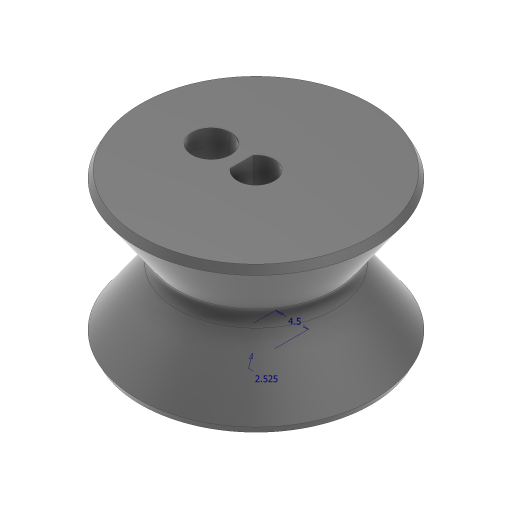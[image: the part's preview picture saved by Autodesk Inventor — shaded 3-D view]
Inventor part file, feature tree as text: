
AUTODESK INVENTOR PART (.ipt)
format: ipt  version: 2023 (Build 270158000, 158)  size: 294,912 bytes
history: native  units: mm
features: sketch x3, chamfer x3, plane x2, revolve x1, extrude x1, sweep x1, fillet x1, hole x1
ambient origin geometry x8: Origin, YZ Plane, XZ Plane, XY Plane, X Axis, Y Axis, Z Axis, Center Point
bodies: Solid1 (feature_tree)
feature tree (13):
  sketch  "Sketch1"  dims[d1=4.5mm d4=20.0mm]
  revolve  "Revolution1"  [1 undecoded]
  extrude  "Extrusion1"  Depth=14.0mm
  chamfer  "Chamfer1"  [1 undecoded]
  plane  "Work Plane3"
  sweep  "Sweep1"
  plane  "Work Plane4"
  fillet  "Fillet1"  Radius=3.490659mm
  chamfer  "Chamfer2"  [1 undecoded]
  hole  "Hole4"  [1 undecoded]
  chamfer  "Chamfer3"  [1 undecoded]
  sketch  "Sketch8"  dims[d5=14.0mm d6=14.0mm]
  sketch  "Sketch9"  dims[d7=90.0deg d8=0.0mm d9=0.0mm d10=1.2mm d11=2.0mm d12=45.0deg d15=30.0deg d20=3.490659mm d71=-12.0mm d72=5.3mm d73=0.0mm d74=0.0mm d92=2.525mm d93=10.0mm d95=2.0mm d98=1.0mm d99=2.0mm d100=45.0deg d102=9.599311mm d103=10.0mm d105=6.5mm d106=6.0mm d107=6.0mm d108=2.0mm d109=90.0deg d110=5.3mm d111=0.0mm d112=0.2mm d113=2.0mm d114=45.0deg]
note: 5 required parameter values undecoded (feature->parameter linkage not recoverable at this tier; creation-order binding heuristic only, values carry confidence <= 0.55)